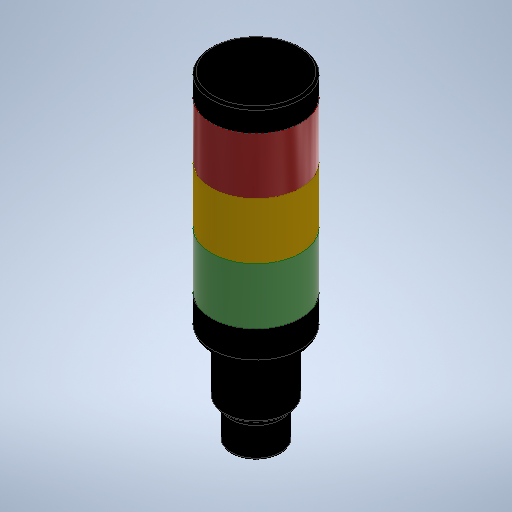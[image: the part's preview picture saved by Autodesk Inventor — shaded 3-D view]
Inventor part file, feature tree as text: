
AUTODESK INVENTOR PART (.ipt)
format: ipt  version: 2025.2 (Build 292293000, 293)  size: 331,776 bytes
history: native  units: mm
features: extrude x8, fillet x5, sketch x4
ambient origin geometry x8: Origin, YZ Plane, XZ Plane, XY Plane, X Axis, Y Axis, Z Axis, Center Point
bodies: Solid1 (feature_tree), Solid2 (feature_tree), Solid3 (feature_tree), Solid4 (feature_tree), Solid5 (feature_tree), Solid6 (feature_tree)
feature tree (17):
  extrude  "Extrusion1"  Depth=16.6mm TaperAngle=0.0deg
  extrude  "Extrusion2"  Depth=25.4mm TaperAngle=0.0deg
  extrude  "Extrusion3"  Depth=3.0mm TaperAngle=0.0deg
  fillet  "Fillet1"  Radius=1.0mm
  fillet  "Fillet2"  Radius=3.0mm
  extrude  "Extrusion4"  Depth=15.0mm TaperAngle=0.0deg
  extrude  "Extrusion5"  Depth=25.0mm TaperAngle=0.0deg
  extrude  "Extrusion6"  Depth=25.0mm TaperAngle=0.0deg
  extrude  "Extrusion7"  Depth=25.0mm TaperAngle=0.0deg
  extrude  "Extrusion8"  Depth=10.0mm TaperAngle=0.0deg
  fillet  "Fillet3"  Radius=1.0mm
  fillet  "Fillet4"  Radius=3.0mm
  fillet  "Fillet5"  Radius=1.0mm
  sketch  "Sketch5"  dims[d0=22.0mm d1=16.6mm d2=0.0mm]
  sketch  "Sketch6"  dims[d3=28.0mm d4=25.4mm d5=0.0mm]
  sketch  "Sketch7"  dims[d6=18.0mm d7=25.4mm d8=0.0mm d9=1.0mm d10=3.0mm]
  sketch  "Sketch8"  dims[d11=39.6mm d12=15.0mm d13=0.0mm d14=25.0mm d15=0.0mm d16=25.0mm d17=0.0mm d18=25.0mm d19=0.0mm d20=10.0mm d21=0.0mm d22=1.0mm d23=3.0mm d24=1.0mm]
